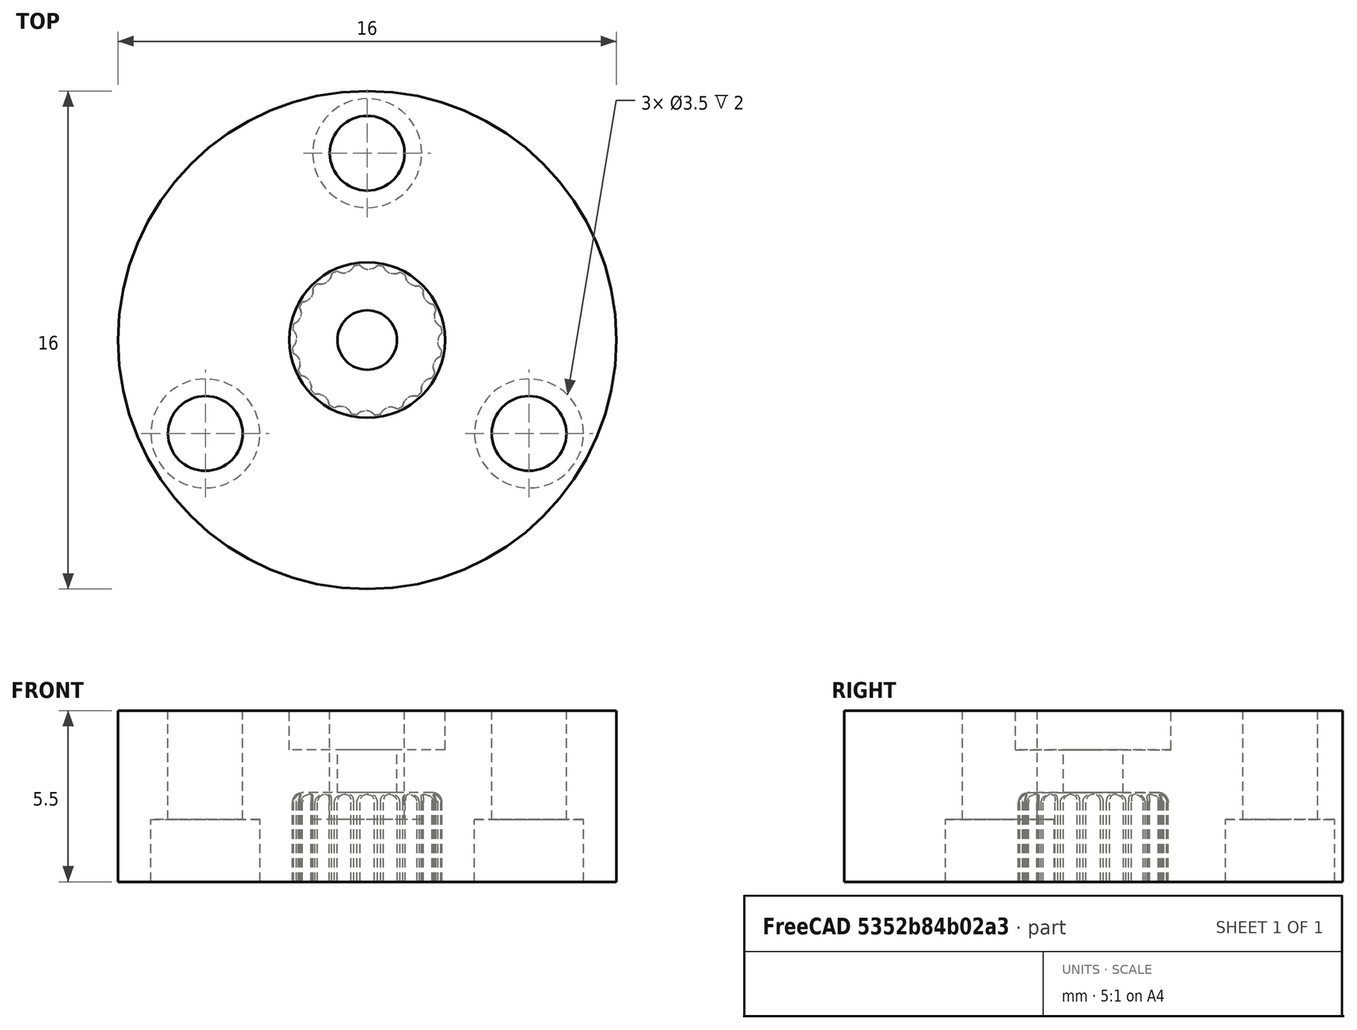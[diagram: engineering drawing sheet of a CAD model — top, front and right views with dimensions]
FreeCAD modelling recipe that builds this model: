
FCSTD DOCUMENT  (FreeCAD 0.17R10802 (Git))
Label: sg90_servo_head
License: All rights reserved
LicenseURL: http://en.wikipedia.org/wiki/All_rights_reserved
objects: Part::Cylinder×12, Part::Cut×11, Part::FeaturePython×2, Part::Fillet×1
note: 26 computed .brp shape members not serialized (recipe doc carries the construction recipe); baked Part::Feature solids carry a one-line shape summary decoded from their .brp

FEATURE [Part::Cylinder] Cylinder006  label="Cilindro002"
  Angle = 360
  AttacherType = Attacher::AttachEngine3D
  Height = 3
  Placement = pos=(2.51021,16.5511,26.9) rot=(0,0,1;0rad)
  Radius = 0.35
FEATURE [Part::FeaturePython] Array  # Draft array (typed FeaturePython)
  Angle = 360
  ArrayType = 1
  Axis = (0,0,1)
  Base = -> Cylinder006
  Center = (0,16.6,0)
  Fuse = false
  IntervalAxis = (0,0,0)
  IntervalX = (1,0,0)
  IntervalY = (0,1,0)
  IntervalZ = (0,0,0)
  NumberPolar = 20
  NumberX = 2
  NumberY = 2
  NumberZ = 1
FEATURE [Part::Cylinder] Cylinder002  label="Cilindro_interior"
  Angle = 360
  AttacherType = Attacher::AttachEngine3D
  Height = 3.2
  Placement = pos=(0,16.6,26.7) rot=(0,0,1;0rad)
  Radius = 2.3
FEATURE [Part::Cylinder] Cylinder005  label="Cilindro_exterior"
  Angle = 360
  AttacherType = Attacher::AttachEngine3D
  Height = 3.2
  Placement = pos=(0,16.6,26.7) rot=(0,0,1;0rad)
  Radius = 0.85
FEATURE [Part::Cut] Cut001  label="Cilindro_vaciado"
  Base = -> Cylinder002
  Tool = -> Cylinder005
FEATURE [Part::Fillet] Fillet
  Base = -> Cut001
  Edges = 1 edges r=0.3: [Edge1]
FEATURE [Part::Cut] Cut002  label="sg90_servo_head"
  Base = -> Fillet
  Placement = pos=(0,-16.6,-26.7) rot=(0,0,1;0rad)
  Tool = -> Array
FEATURE [Part::FeaturePython] Scale  label="head_scaled_1.05"  # Draft clone (typed FeaturePython)
  Objects = -> [Cut002]
  Placement = pos=(0,-17.43,-28.035) rot=(0,0,1;0rad)
  Scale = (1.05,1.05,1.05)
FEATURE [Part::Cylinder] Cylinder  label="horn_cylinder"
  Angle = 360
  AttacherType = Attacher::AttachEngine3D
  Height = 5.5
  Placement = pos=(0,0,0.5) rot=(0,0,1;0rad)
  Radius = 8
FEATURE [Part::Cut] Cut  label="horn_no_holes"
  Base = -> Cylinder
  Tool = -> Scale
FEATURE [Part::Cylinder] Cylinder007  label="m3_screwhole"
  Angle = 360
  AttacherType = Attacher::AttachEngine3D
  Height = 10
  Placement = pos=(0,6,0) rot=(0,0,1;0rad)
  Radius = 1.2
FEATURE [Part::Cylinder] Cylinder008  label="m3_screwhole001"
  Angle = 360
  AttacherType = Attacher::AttachEngine3D
  Height = 10
  Placement = pos=(-5.19615,-3,0) rot=(0,0,1;2.0944rad)
  Radius = 1.2
FEATURE [Part::Cylinder] Cylinder009  label="m3_screwhole002"
  Angle = 360
  AttacherType = Attacher::AttachEngine3D
  Height = 10
  Placement = pos=(5.19615,-3,0) rot=(0,0,-1;2.0944rad)
  Radius = 1.2
FEATURE [Part::Cylinder] Cylinder010  label="screw_head_recess"
  Angle = 360
  AttacherType = Attacher::AttachEngine3D
  Height = 10
  Placement = pos=(0,0,4.74) rot=(0,0,1;0rad)
  Radius = 2.5
FEATURE [Part::Cylinder] Cylinder011  label="center_screw"
  Angle = 360
  AttacherType = Attacher::AttachEngine3D
  Height = 10
  Radius = 0.955
FEATURE [Part::Cut] Cut003  label="horn_center_hole"
  Base = -> Cut
  Tool = -> Cylinder011
FEATURE [Part::Cut] Cut004  label="without_adapter_holes"
  Base = -> Cut003
  Tool = -> Cylinder010
FEATURE [Part::Cylinder] Cylinder012  label="m3_screwhole002_recess"
  Angle = 360
  AttacherType = Attacher::AttachEngine3D
  Height = 2.5
  Placement = pos=(0,6,0) rot=(0,0,1;0rad)
  Radius = 1.75
FEATURE [Part::Cylinder] Cylinder013  label="m3_screwhole001_recess"
  Angle = 360
  AttacherType = Attacher::AttachEngine3D
  Height = 2.5
  Placement = pos=(-5.19615,-3,0) rot=(0,0,1;2.0944rad)
  Radius = 1.75
FEATURE [Part::Cylinder] Cylinder014  label="m3_screwhole_recess"
  Angle = 360
  AttacherType = Attacher::AttachEngine3D
  Height = 2.5
  Placement = pos=(5.19615,-3,0) rot=(0,0,-1;2.0944rad)
  Radius = 1.75
FEATURE [Part::Cut] Cut005
  Base = -> Cut004
  Tool = -> Cylinder008
FEATURE [Part::Cut] Cut006
  Base = -> Cut005
  Tool = -> Cylinder009
FEATURE [Part::Cut] Cut007
  Base = -> Cut006
  Tool = -> Cylinder007
FEATURE [Part::Cut] Cut008
  Base = -> Cut007
  Tool = -> Cylinder014
FEATURE [Part::Cut] Cut009
  Base = -> Cut008
  Tool = -> Cylinder013
FEATURE [Part::Cut] Cut010  label="sg90_servo_horn"
  Base = -> Cut009
  Tool = -> Cylinder012
